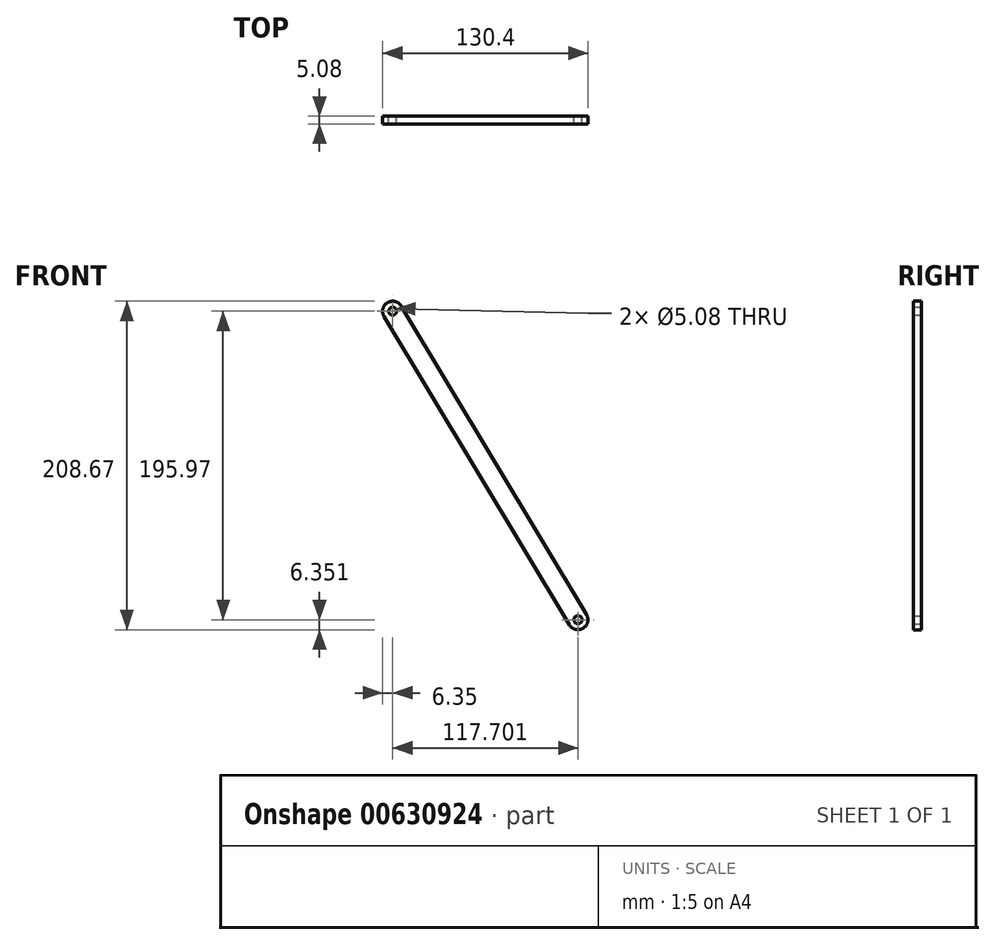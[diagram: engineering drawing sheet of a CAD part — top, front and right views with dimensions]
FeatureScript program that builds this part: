
annotation { "Feature Type Name" : "Feature", "Feature Type Description" : "" }
export const myFeature = defineFeature(function(context is Context, id is Id, definition is map)
    precondition{}
    {
        {
            var Q0;
            Q0=qCreatedBy(makeId("Front.planeOp"),FACE);
            var sketch = newSketch(context, id + "F0", { "sketchPlane" : qUnion([Q0])});
            skCircle(sketch, "E0", {"center": v(-30.44, 57.02) * mm, "radius": 6.35 * mm});
            skCircle(sketch, "E1", {"center": v(87.26, -138.95) * mm, "radius": 6.35 * mm});
            skCircle(sketch, "E2", {"center": v(-30.44, 57.02) * mm, "radius": 2.54 * mm});
            skCircle(sketch, "E3", {"center": v(87.26, -138.95) * mm, "radius": 2.54 * mm});
            skLineSegment(sketch, "E4", {"start": v(-35.88, 53.75) * mm, "end": v(81.82, -142.22) * mm});
            skLineSegment(sketch, "E5", {"start": v(-25, 60.3) * mm, "end": v(92.7, -135.68) * mm});
            skSolve(sketch);
        }
        {
            var Q0;
            Q0 = qSketchRegion(id + "F0", true);
            extrude(context, id + "F1", {"entities" : qUnion([Q0]), "depth" : 5.08 * mm, "offsetDistance" : 25.4 * mm});
        }
    });
